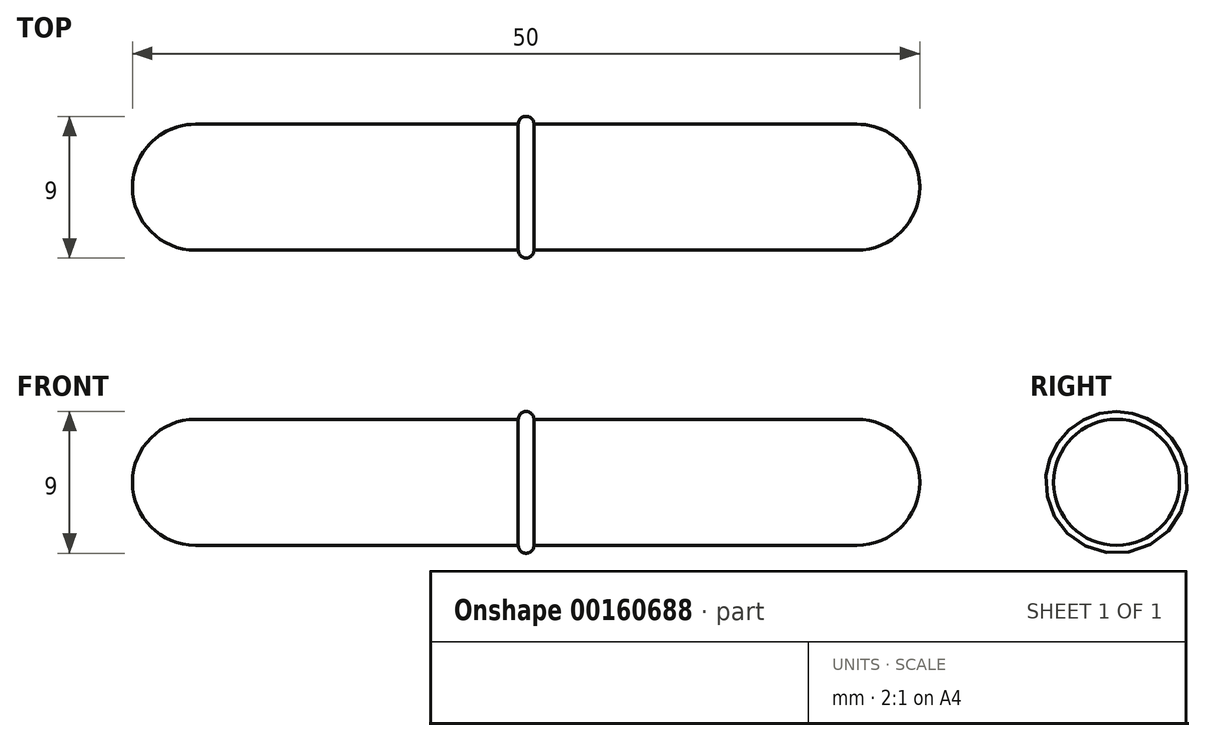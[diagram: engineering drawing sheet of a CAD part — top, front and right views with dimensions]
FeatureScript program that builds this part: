
annotation { "Feature Type Name" : "Feature", "Feature Type Description" : "" }
export const myFeature = defineFeature(function(context is Context, id is Id, definition is map)
    precondition{}
    {
        {
            var Q0;
            Q0=qCreatedBy(makeId("Top.planeOp"),FACE);
            var sketch = newSketch(context, id + "F0", { "sketchPlane" : qUnion([Q0])});
            skLineSegment(sketch, "E0", {"start": v(0, 0) * mm, "end": v(21, 0) * mm});
            skArc(sketch, "E1", {"start": v(25, 0) * mm, "mid": v(23.83, 2.83) * mm, "end": v(21, 4) * mm});
            skLineSegment(sketch, "E2", {"start": v(21, 4) * mm, "end": v(0, 4) * mm});
            skArc(sketch, "E3", {"start": v(0.5, 4) * mm, "mid": v(0.35, 4.35) * mm, "end": v(0, 4.5) * mm});
            skLineSegment(sketch, "E4", {"start": v(25, 0) * mm, "end": v(21, 0) * mm});
            skLineSegment(sketch, "E5", {"start": v(0, 4.5) * mm, "end": v(0, 0) * mm});
            skSolve(sketch);
        }
        {
            var Q0;
            Q0=qSketchRegion(id+"F0",true);
            var Q1;
            Q1=sQuery(id+"F0.wireOp",EDGE,"E0");
            revolve(context, id + "F1", {"entities" : qUnion([Q0]), "axis" : qUnion([Q1]), "revolveType" : RevolveType.FULL});
        }
        {
            var Q0;
            Q0=makeQuery(id+"F1.opRevolve","SWEPT_BODY",BODY,{"disambiguationData":[OSD([sQuery(id+"F0.wireOp",EDGE,"E0"),sQuery(id+"F0.wireOp",EDGE,"E1"),sQuery(id+"F0.wireOp",EDGE,"E2"),sQuery(id+"F0.wireOp",EDGE,"E3"),sQuery(id+"F0.wireOp",EDGE,"E4"),sQuery(id+"F0.wireOp",EDGE,"E5")])]});
            var Q1;
            Q1=makeQuery(id+"F1.opRevolve","SWEPT_FACE",FACE,{"disambiguationData":[OSD([sQuery(id+"F0.wireOp",EDGE,"E5")])]});
            mirror(context, id + "F2", {"operationType" : NewBodyOperationType.ADD, "entities" : qUnion([Q0]), "mirrorPlane" : qUnion([Q1])});
        }
        {
            var Q0;
            Q0=qCreatedBy(makeId("Front.planeOp"),FACE);
            var sketch = newSketch(context, id + "F3", { "sketchPlane" : qUnion([Q0])});
            skLineSegment(sketch, "E6", {"start": v(0, 0) * mm, "end": v(0, 4.74) * mm, "construction": true});
            skSolve(sketch);
        }
    });
